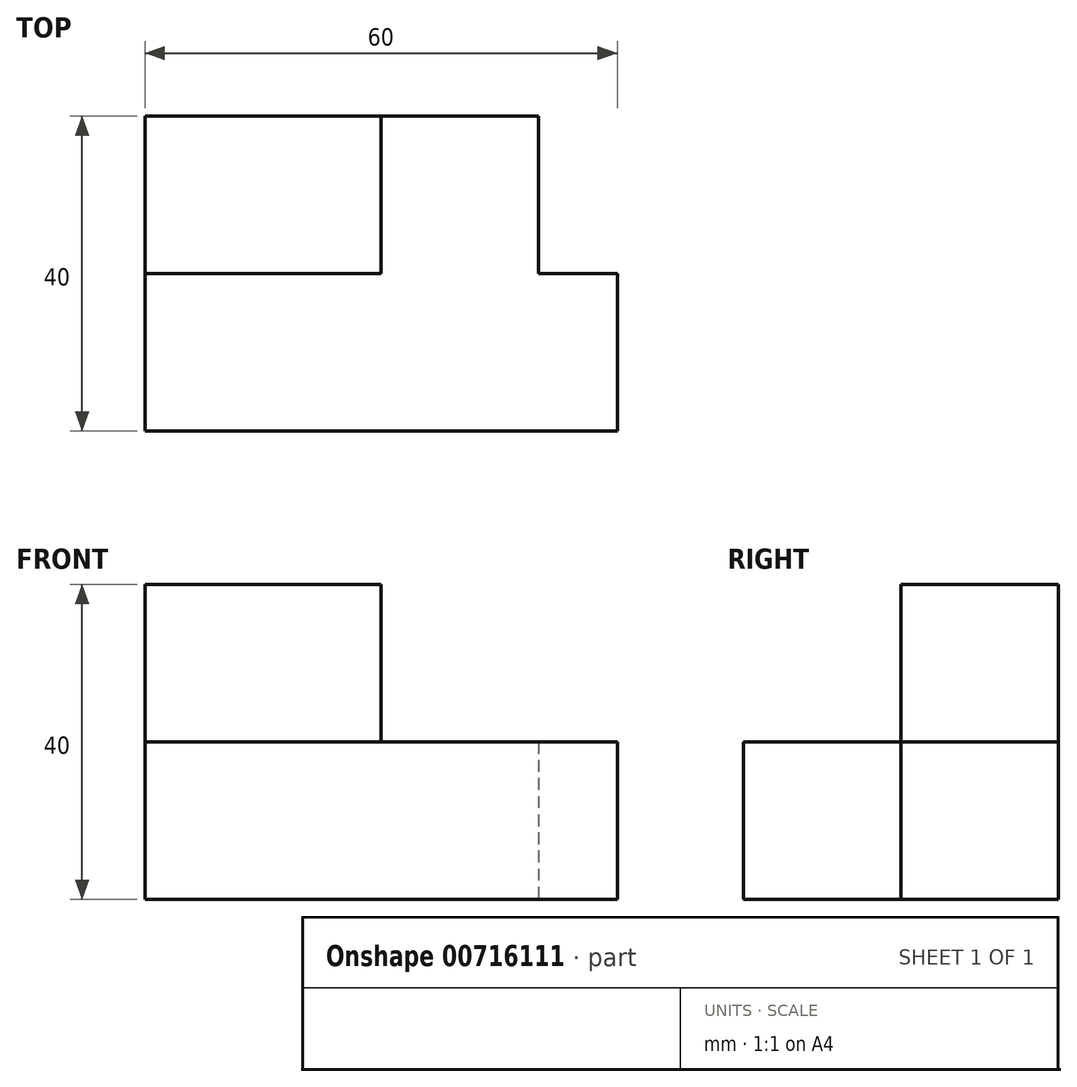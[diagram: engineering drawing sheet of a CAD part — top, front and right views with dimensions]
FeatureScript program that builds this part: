
annotation { "Feature Type Name" : "Feature", "Feature Type Description" : "" }
export const myFeature = defineFeature(function(context is Context, id is Id, definition is map)
    precondition{}
    {
        {
            var Q0;
            Q0=qCreatedBy(makeId("Top.planeOp"),FACE);
            var sketch = newSketch(context, id + "F0", { "sketchPlane" : qUnion([Q0])});
            skLineSegment(sketch, "E0", {"start": v(0, 0) * mm, "end": v(60, 0) * mm});
            skLineSegment(sketch, "E1", {"start": v(60, 0) * mm, "end": v(60, 20) * mm});
            skLineSegment(sketch, "E2", {"start": v(60, 20) * mm, "end": v(50, 20) * mm});
            skLineSegment(sketch, "E3", {"start": v(50, 20) * mm, "end": v(50, 40) * mm});
            skLineSegment(sketch, "E4", {"start": v(50, 40) * mm, "end": v(0, 40) * mm});
            skLineSegment(sketch, "E5", {"start": v(0, 40) * mm, "end": v(0, 0) * mm});
            skSolve(sketch);
        }
        {
            var Q0;
            Q0 = qSketchRegion(id + "F0", true);
            extrude(context, id + "F1", {"entities" : qUnion([Q0]), "depth" : 20 * mm, "offsetDistance" : 25 * mm});
        }
        {
            var Q0;
            Q0=makeQuery(id+"F1.opExtrude","CAP_FACE",FACE,{"disambiguationData":[OSD([sQuery(id+"F0.wireOp",EDGE,"E0"),sQuery(id+"F0.wireOp",EDGE,"E1"),sQuery(id+"F0.wireOp",EDGE,"E2"),sQuery(id+"F0.wireOp",EDGE,"E3"),sQuery(id+"F0.wireOp",EDGE,"E4"),sQuery(id+"F0.wireOp",EDGE,"E5")])],"isStart":false});
            var sketch = newSketch(context, id + "F2", { "sketchPlane" : qUnion([Q0])});
            skLineSegment(sketch, "E6.bottom", {"start": v(0, 40) * mm, "end": v(30, 40) * mm});
            skLineSegment(sketch, "E6.top", {"start": v(0, 20) * mm, "end": v(30, 20) * mm});
            skLineSegment(sketch, "E6.left", {"start": v(0, 40) * mm, "end": v(0, 20) * mm});
            skLineSegment(sketch, "E6.right", {"start": v(30, 40) * mm, "end": v(30, 20) * mm});
            skSolve(sketch);
        }
        {
            var Q0;
            Q0 = qSketchRegion(id + "F2", true);
            extrude(context, id + "F3", {"entities" : qUnion([Q0]), "operationType" : NewBodyOperationType.ADD, "depth" : 20 * mm, "offsetDistance" : 25 * mm});
        }
    });
